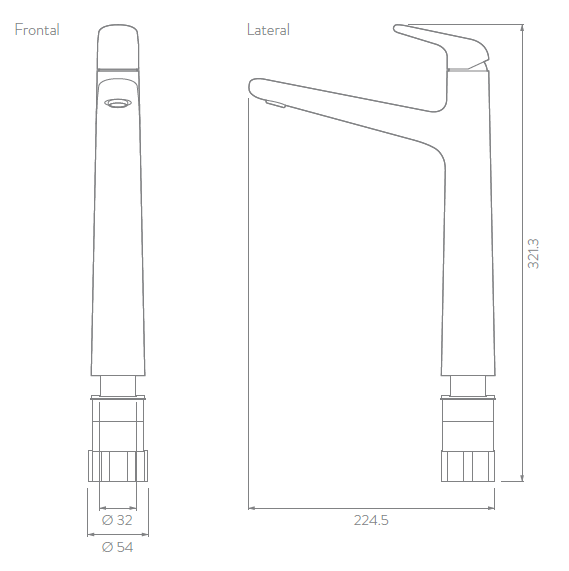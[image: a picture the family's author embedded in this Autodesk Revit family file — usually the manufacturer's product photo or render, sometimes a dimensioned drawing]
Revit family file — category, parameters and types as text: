
# Revit family: LQ1065551_Grifería para Lavamanos Monocontrol Liquid Niquel Alta
name_source: partatom
category: Plumbing Fixtures
units: mm (PartAtom-declared; Revit-internal decimal feet)

## family parameters
Always vertical = Yes
Cut with Voids When Loaded = No
OmniClass Number = 23.31.11.00
OmniClass Title = Faucets
Part Type = Normal
Room Calculation Point = No
Round Connector Dimension = Use Diameter
Shared = No
Work Plane-Based = No

## types (1)
- LQ1065551_Grifería para Lavamanos Monocontrol Liquid Niquel Alta
    Acabado = Corona_Niquel
    Alto = 321 mm  [stored 1.05315 ft]
    Altura de la grifería = Alta
    Ancho = 54 mm  [stored 0.177165 ft]
    Capacidad de flujo = 60 psi: 4,4 L/min
    Colección = Liquid
    Consumo de agua = 5.7 lt
    Creado por = IDD
    Description = La línea de griferías, duchas y accesorios Liquid se inspira en la tensión superficial del agua y en cómo esta crea formas armoniosas adaptándose al ambiente. Al igual que el agua, las superficies de las griferías Liquid juegan con la luz y los reflejos que fluyen alrededorde sus formas, sus líneas continuas y simplicidad formal proporcionan la ventaja práctica y limpieza sin esfuerzo.
Incluye la tecnología Ecostream, de ahorro de agua; y la tecnología ThermoControl, de control más preciso de la temperatura.
Incluye apertura con accionamiento central en frío que evita el encendido automático de calentadores y calderas ahorrando energía; además, es de fácil limpieza gracias al diseño que evita la acumulación de impurezas, es resistente a la corrosión, pelado y decoloración por agua y tiene recubrimientos no tóxicos.
    Fecha de creación = 09/10/2020
    Garantía = 30 años en estructura
    Garantías de otros componentes = 5 años en acabados
    Incluye = Cuerpo, Manija
    Linea = Liquid
    Longitud = 225 mm  [stored 0.738189 ft]
    Material = Metálico
    Peso  Bruto = 2.200 g. - 4,85 lb.
    Peso neto = 2.000 g. - 4,41 lb.
    Presión máxima recomendada = 125 psi (860 Kpa)
    Presión mínima recomendada = 20 psi (140 Kpa)
    Productos compatibles = Lavamanos tipo vessel
    Resistencia = Resistente a la corrosión pelado y decoloración por agua
    Sistema de accionamiento = Palanca monocontrol
    Tecnologías = DuraCrome EcoStream ThermoControl
    Temperaturas máxima de trabajo = 71°C / 159,8°F
    Temperaturas mínima de trabajo = 5°C / 41 °F
    Tipo de Chorro = Espumoso
    Tipo de Grifería = Monocontrol
    Tipo de manija/accionamiento = Palanca
    URL = https://corona.co
    Uso = Residencial
    Vida útil = 500.000 ciclos.

note: [stored X ft] marks values corroborated as IEEE doubles in the binary element streams (Revit-internal decimal feet)

## geometry (parser evidence)
native form markers: Sweep x7
no freeform markers — native parametric forms only
